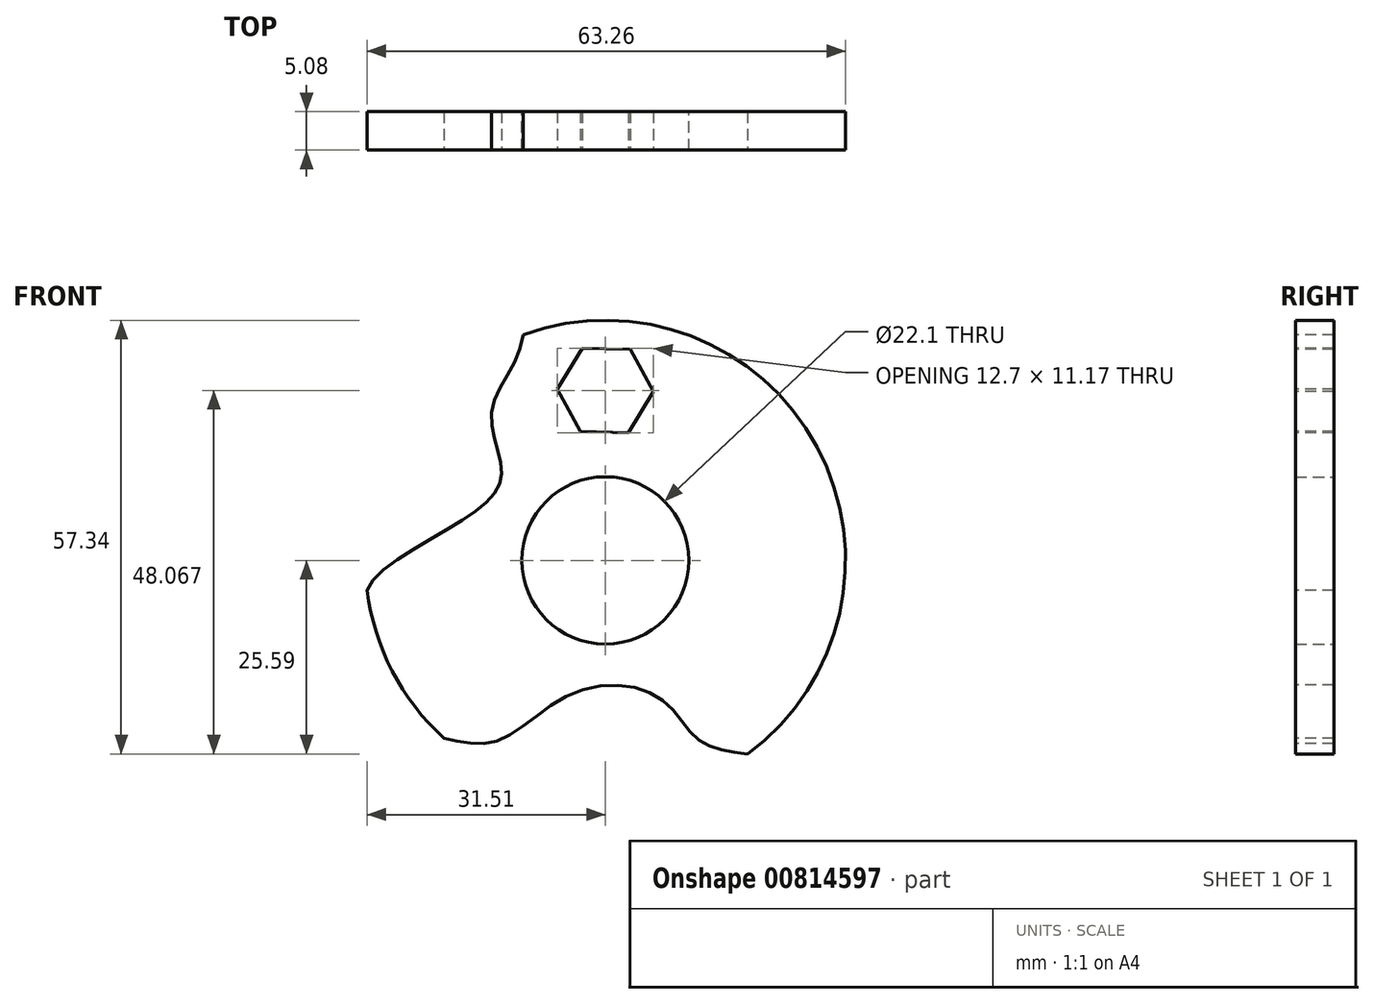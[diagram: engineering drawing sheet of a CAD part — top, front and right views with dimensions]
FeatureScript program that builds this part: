
annotation { "Feature Type Name" : "Feature", "Feature Type Description" : "" }
export const myFeature = defineFeature(function(context is Context, id is Id, definition is map)
    precondition{}
    {
        {
            var Q0;
            Q0=qCreatedBy(makeId("Front.planeOp"),FACE);
            var sketch = newSketch(context, id + "F0", { "sketchPlane" : qUnion([Q0])});
            skCircle(sketch, "E0", {"center": v(0, 0) * mm, "radius": 31.75 * mm});
            skCircle(sketch, "E1", {"center": v(0, 0) * mm, "radius": 11.05 * mm});
            skSolve(sketch);
        }
        {
            var Q0;
            Q0=makeQuery(id+"F0.imprint","IMPRINT",FACE,{"disambiguationData":[TD([[makeQuery(id+"F0.imprint","IMPRINT",EDGE,{"derivedFrom":sQuery(id+"F0.wireOp",EDGE,"E0")}),1.0]])]});
            extrude(context, id + "F1", {"entities" : qUnion([Q0]), "depth" : 5.08 * mm, "offsetDistance" : 25.4 * mm});
        }
        {
            var Q0;
            Q0=makeQuery(id+"F1.opExtrude","CAP_FACE",FACE,{"disambiguationData":[OSD([sQuery(id+"F0.wireOp",EDGE,"E0"),sQuery(id+"F0.wireOp",EDGE,"E1")])],"isStart":false});
            var sketch = newSketch(context, id + "F2", { "sketchPlane" : qUnion([Q0])});
            skCircle(sketch, "E2.cCircle", {"center": v(0, 22.48) * mm, "radius": 5.5 * mm, "construction": true});
            skLineSegment(sketch, "E2.0", {"start": v(-3.32, 17.07) * mm, "end": v(-6.35, 22.65) * mm});
            skLineSegment(sketch, "E2.1", {"start": v(-6.35, 22.65) * mm, "end": v(-3.02, 28.06) * mm});
            skLineSegment(sketch, "E2.2", {"start": v(-3.02, 28.06) * mm, "end": v(3.32, 27.89) * mm});
            skLineSegment(sketch, "E2.3", {"start": v(3.32, 27.89) * mm, "end": v(6.35, 22.3) * mm});
            skLineSegment(sketch, "E2.4", {"start": v(6.35, 22.3) * mm, "end": v(3.02, 16.9) * mm});
            skLineSegment(sketch, "E2.5", {"start": v(3.02, 16.9) * mm, "end": v(-3.32, 17.07) * mm});
            skPoint(sketch, "E2.0.midPoint", {"position": v(-4.84, 19.86) * mm});
            skSolve(sketch);
        }
        {
            var Q0;
            Q0=makeQuery(id+"F2.imprint","IMPRINT",FACE,{"disambiguationData":[TD([[makeQuery(id+"F2.imprint","IMPRINT",EDGE,{"derivedFrom":sQuery(id+"F2.wireOp",EDGE,"E2.0")}),-1.0]])]});
            extrude(context, id + "F3", {"entities" : qUnion([Q0]), "operationType" : NewBodyOperationType.REMOVE, "oppositeDirection" : true, "depth" : 25.4 * mm, "offsetDistance" : 25.4 * mm});
        }
        {
            var Q0;
            Q0=makeQuery(id+"F1.opExtrude","CAP_FACE",FACE,{"disambiguationData":[OSD([sQuery(id+"F0.wireOp",EDGE,"E0"),sQuery(id+"F0.wireOp",EDGE,"E1")])],"isStart":false});
            var sketch = newSketch(context, id + "F4", { "sketchPlane" : qUnion([Q0])});
            skFitSpline(sketch, "E3", {"points": [v(-29.97, -10.49) * mm, v(-31.5, -3.93) * mm, v(-18.97, 5.28) * mm, v(-13.7, 11.55) * mm, v(-15.01, 19.8) * mm, v(-10.89, 29.83) * mm, v(-17.65, 37.28) * mm, v(-45.7, -2.64) * mm, v(-33.49, -17.82) * mm, v(-29.97, -10.49) * mm]});
            skSolve(sketch);
        }
        {
            var Q0;
            {var subQ0=sQuery(id+"F4.wireOp",EDGE,"E3");var subQ1=makeQuery(id+"F1.opExtrude","CAP_EDGE",EDGE,{"disambiguationData":[OSD([sQuery(id+"F0.wireOp",EDGE,"E0")])],"isStart":false});var subQ2=makeQuery(id+"F4.imprint","INTERSECT",VERTEX,{"disambiguationData":[OD(1.0)],"derivedFrom":[subQ1,subQ0]});Q0=makeQuery(id+"F4.imprint","IMPRINT",FACE,{"disambiguationData":[TD([[makeQuery(id+"F4.imprint","IMPRINT",EDGE,{"disambiguationData":[TD([[subQ2,1.0]])],"derivedFrom":subQ0}),1.0]])]});}
            extrude(context, id + "F5", {"entities" : qUnion([Q0]), "operationType" : NewBodyOperationType.REMOVE, "oppositeDirection" : true, "depth" : 25.4 * mm, "offsetDistance" : 25.4 * mm});
        }
        {
            var Q0;
            Q0=makeQuery(id+"F1.opExtrude","CAP_FACE",FACE,{"disambiguationData":[OSD([sQuery(id+"F0.wireOp",EDGE,"E0"),sQuery(id+"F0.wireOp",EDGE,"E1")])],"isStart":false});
            var sketch = newSketch(context, id + "F6", { "sketchPlane" : qUnion([Q0])});
            skFitSpline(sketch, "E4", {"points": [v(10.2, 30.07) * mm, v(16.66, 23.43) * mm, v(13.03, 13.2) * mm, v(21.61, 2.97) * mm, v(27.88, -5.83) * mm, v(29, -12.93) * mm, v(29.63, -11.41) * mm], "startDerivative": vector(54.85, -33.23) * mm, "endDerivative": vector(9.81, 31.87) * mm});
            skSolve(sketch);
        }
        {
            var Q0;
            {var subQ0=sQuery(id+"F6.wireOp",EDGE,"E4");var subQ1=makeQuery(id+"F1.opExtrude","CAP_EDGE",EDGE,{"disambiguationData":[OSD([sQuery(id+"F0.wireOp",EDGE,"E0")])],"isStart":false});var subQ2=makeQuery(id+"F6.imprint","INTERSECT",VERTEX,{"disambiguationData":[OD(0.0)],"derivedFrom":[subQ1,subQ0]});Q0=makeQuery(id+"F6.imprint","IMPRINT",FACE,{"disambiguationData":[TD([[makeQuery(id+"F6.imprint","IMPRINT",EDGE,{"disambiguationData":[TD([[subQ2,-1.0]])],"derivedFrom":subQ0}),1.0]])]});}
            extrude(context, id + "F7", {"entities" : qUnion([Q0]), "operationType" : NewBodyOperationType.REMOVE, "oppositeDirection" : true, "depth" : 25.4 * mm, "offsetDistance" : 25.4 * mm});
        }
        {
            var Q0;
            Q0=makeQuery(id+"F1.opExtrude","CAP_FACE",FACE,{"disambiguationData":[OSD([sQuery(id+"F0.wireOp",EDGE,"E0"),sQuery(id+"F0.wireOp",EDGE,"E1")])],"isStart":false});
            var sketch = newSketch(context, id + "F8", { "sketchPlane" : qUnion([Q0])});
            skPoint(sketch, "E5.6.internal.snap0", {"position": v(19.32, -16.74) * mm});
            skFitSpline(sketch, "E6", {"points": [v(-21.35, -23.5) * mm, v(-14.02, -23.76) * mm, v(-4.12, -17.49) * mm, v(7.1, -18.15) * mm, v(12.37, -23.76) * mm, v(18.8, -25.6) * mm], "startDerivative": vector(40.34, -9.63) * mm, "endDerivative": vector(40.51, -4.39) * mm});
            skSolve(sketch);
        }
        {
            var Q0;
            {var subQ0=sQuery(id+"F8.wireOp",EDGE,"E6");Q0=makeQuery(id+"F8.imprint","IMPRINT",FACE,{"disambiguationData":[TD([[makeQuery(id+"F8.imprint","IMPRINT",EDGE,{"derivedFrom":subQ0}),-1.0]])]});}
            extrude(context, id + "F9", {"entities" : qUnion([Q0]), "operationType" : NewBodyOperationType.REMOVE, "oppositeDirection" : true, "depth" : 25.4 * mm, "offsetDistance" : 25.4 * mm});
        }
    });
